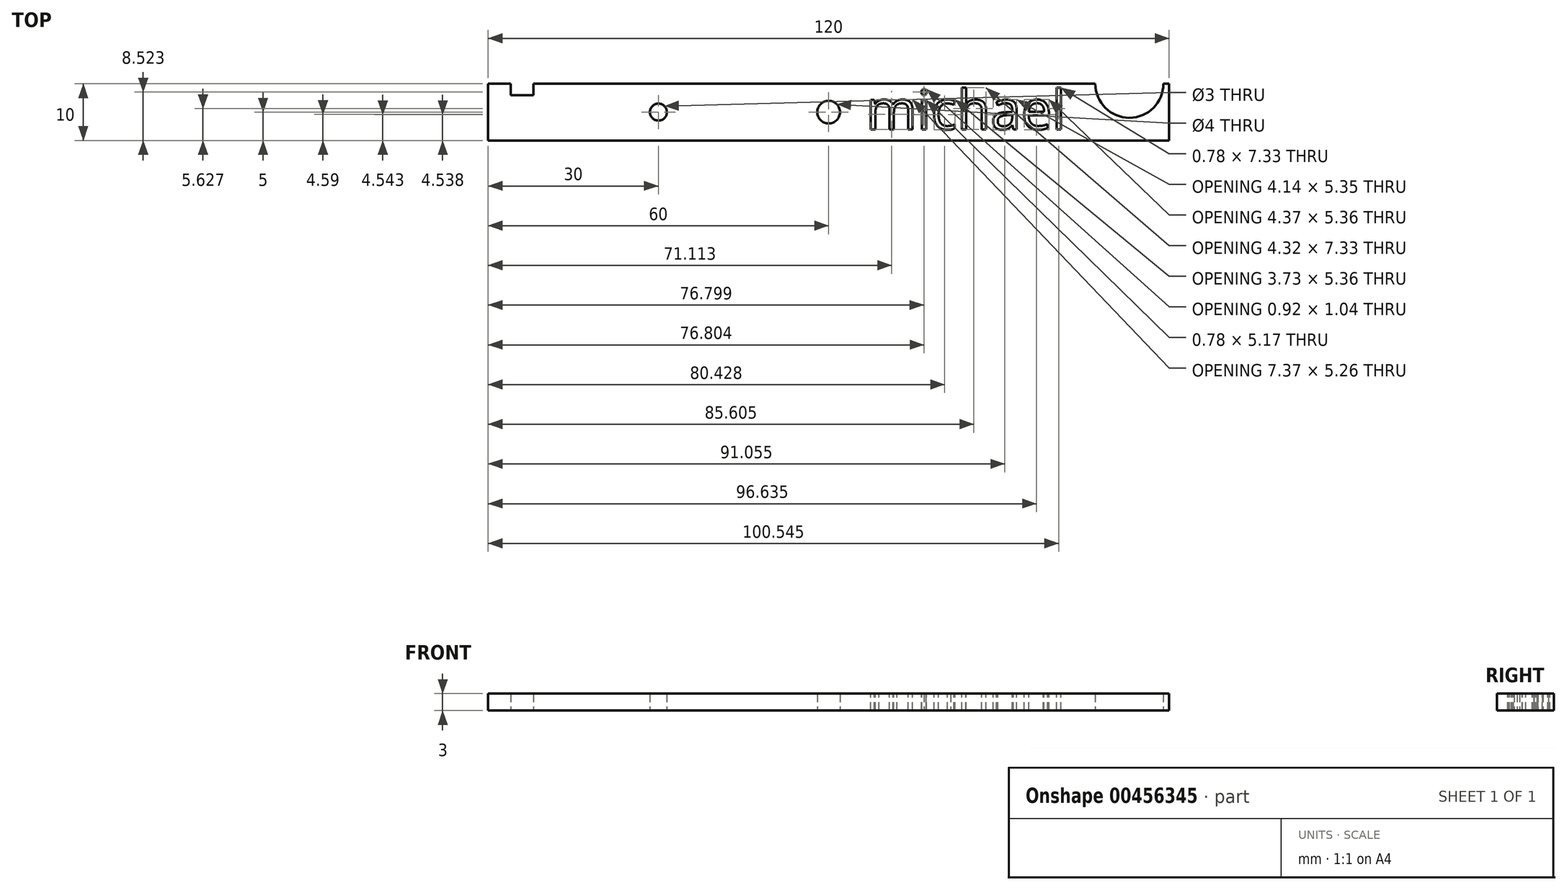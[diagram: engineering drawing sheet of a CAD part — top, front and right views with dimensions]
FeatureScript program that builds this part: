
annotation { "Feature Type Name" : "Feature", "Feature Type Description" : "" }
export const myFeature = defineFeature(function(context is Context, id is Id, definition is map)
    precondition{}
    {
        {
            var Q0;
            Q0=qCreatedBy(makeId("Top.planeOp"),FACE);
            var sketch = newSketch(context, id + "F0", { "sketchPlane" : qUnion([Q0])});
            skLineSegment(sketch, "E0.bottom", {"start": v(60, -5) * mm, "end": v(-60, -5) * mm});
            skLineSegment(sketch, "E0.top", {"start": v(60, 5) * mm, "end": v(-60, 5) * mm});
            skLineSegment(sketch, "E0.left", {"start": v(60, -5) * mm, "end": v(60, 5) * mm});
            skLineSegment(sketch, "E0.right", {"start": v(-60, -5) * mm, "end": v(-60, 5) * mm});
            skPoint(sketch, "E0.middle", {"position": v(0, 0) * mm});
            skLineSegment(sketch, "E1.bottom", {"start": v(-56, 5) * mm, "end": v(-52, 5) * mm});
            skLineSegment(sketch, "E1.top", {"start": v(-56, 3) * mm, "end": v(-52, 3) * mm});
            skLineSegment(sketch, "E1.left", {"start": v(-56, 5) * mm, "end": v(-56, 3) * mm});
            skLineSegment(sketch, "E1.right", {"start": v(-52, 5) * mm, "end": v(-52, 3) * mm});
            skCircle(sketch, "E2", {"center": v(0, 0) * mm, "radius": 2 * mm});
            skCircle(sketch, "E3", {"center": v(0, 0) * mm, "radius": 7 * mm});
            skCircle(sketch, "E4", {"center": v(-30, 0) * mm, "radius": 1.5 * mm});
            skCircle(sketch, "E5", {"center": v(53, 5) * mm, "radius": 6 * mm});
            skSolve(sketch);
        }
        {
            var Q0;
            {var subQ0=sQuery(id+"F0.wireOp",EDGE,"E0.right");Q0=makeQuery(id+"F0.imprint","IMPRINT",FACE,{"disambiguationData":[TD([[makeQuery(id+"F0.imprint","IMPRINT",EDGE,{"derivedFrom":subQ0}),-1.0]])]});}
            var Q1;
            {var subQ0=sQuery(id+"F0.wireOp",EDGE,"E0.left");Q1=makeQuery(id+"F0.imprint","IMPRINT",FACE,{"disambiguationData":[TD([[makeQuery(id+"F0.imprint","IMPRINT",EDGE,{"derivedFrom":subQ0}),1.0]])]});}
            var Q2;
            Q2=makeQuery(id+"F0.imprint","IMPRINT",FACE,{"disambiguationData":[TD([[makeQuery(id+"F0.imprint","IMPRINT",EDGE,{"derivedFrom":sQuery(id+"F0.wireOp",EDGE,"E2")}),-1.0]])]});
            extrude(context, id + "F1", {"entities" : qUnion([Q0, Q1, Q2]), "depth" : 3 * mm});
        }
        {
            var Q0;
            Q0=makeQuery(id+"F1.opExtrude","CAP_FACE",FACE,{"disambiguationData":[OSD([sQuery(id+"F0.wireOp",EDGE,"E0.bottom"),sQuery(id+"F0.wireOp",EDGE,"E0.top"),sQuery(id+"F0.wireOp",EDGE,"E0.left"),sQuery(id+"F0.wireOp",EDGE,"E0.right"),sQuery(id+"F0.wireOp",EDGE,"E1.top"),sQuery(id+"F0.wireOp",EDGE,"E1.left"),sQuery(id+"F0.wireOp",EDGE,"E1.right"),sQuery(id+"F0.wireOp",EDGE,"E2"),sQuery(id+"F0.wireOp",EDGE,"E4"),sQuery(id+"F0.wireOp",EDGE,"E5")])],"isStart":false});
            var sketch = newSketch(context, id + "F2", { "sketchPlane" : qUnion([Q0])});
            skText(sketch, "E6", { "text": "michael", "fontName": "OpenSans-Regular.ttf"});
            const initialGuessF2  = {"E6": [0.0066, -0.00304, 1, 0, 0.00695]};
            skSetInitialGuess(sketch, initialGuessF2);
            skSolve(sketch);
        }
        {
            var Q0;
            Q0=makeQuery(id+"F2.imprint","IMPRINT",FACE,{"disambiguationData":[TD([[makeQuery(id+"F2.imprint","IMPRINT",EDGE,{"derivedFrom":sQuery(id+"F2.wireOp",EDGE,"E6.sketch_text.stroke-0")}),-1.0]])]});
            var Q1;
            Q1=makeQuery(id+"F2.imprint","IMPRINT",FACE,{"disambiguationData":[TD([[makeQuery(id+"F2.imprint","IMPRINT",EDGE,{"derivedFrom":sQuery(id+"F2.wireOp",EDGE,"E6.sketch_text.stroke-28")}),-1.0]])]});
            var Q2;
            Q2=makeQuery(id+"F2.imprint","IMPRINT",FACE,{"disambiguationData":[TD([[makeQuery(id+"F2.imprint","IMPRINT",EDGE,{"derivedFrom":sQuery(id+"F2.wireOp",EDGE,"E6.sketch_text.stroke-32")}),-1.0]])]});
            var Q3;
            Q3=makeQuery(id+"F2.imprint","IMPRINT",FACE,{"disambiguationData":[TD([[makeQuery(id+"F2.imprint","IMPRINT",EDGE,{"derivedFrom":sQuery(id+"F2.wireOp",EDGE,"E6.sketch_text.stroke-40")}),-1.0]])]});
            var Q4;
            Q4=makeQuery(id+"F2.imprint","IMPRINT",FACE,{"disambiguationData":[TD([[makeQuery(id+"F2.imprint","IMPRINT",EDGE,{"derivedFrom":sQuery(id+"F2.wireOp",EDGE,"E6.sketch_text.stroke-55")}),-1.0]])]});
            var Q5;
            Q5=makeQuery(id+"F2.imprint","IMPRINT",FACE,{"disambiguationData":[TD([[makeQuery(id+"F2.imprint","IMPRINT",EDGE,{"derivedFrom":sQuery(id+"F2.wireOp",EDGE,"E6.sketch_text.stroke-73")}),-1.0]])]});
            var Q6;
            Q6=makeQuery(id+"F2.imprint","IMPRINT",FACE,{"disambiguationData":[TD([[makeQuery(id+"F2.imprint","IMPRINT",EDGE,{"derivedFrom":sQuery(id+"F2.wireOp",EDGE,"E6.sketch_text.stroke-119")}),-1.0]])]});
            var Q7;
            Q7=makeQuery(id+"F2.imprint","IMPRINT",FACE,{"disambiguationData":[TD([[makeQuery(id+"F2.imprint","IMPRINT",EDGE,{"derivedFrom":sQuery(id+"F2.wireOp",EDGE,"E6.sketch_text.stroke-100")}),-1.0]])]});
            extrude(context, id + "F3", {"entities" : qUnion([Q0, Q1, Q2, Q3, Q4, Q5, Q6, Q7]), "operationType" : NewBodyOperationType.REMOVE, "oppositeDirection" : true, "depth" : 25 * mm});
        }
    });
